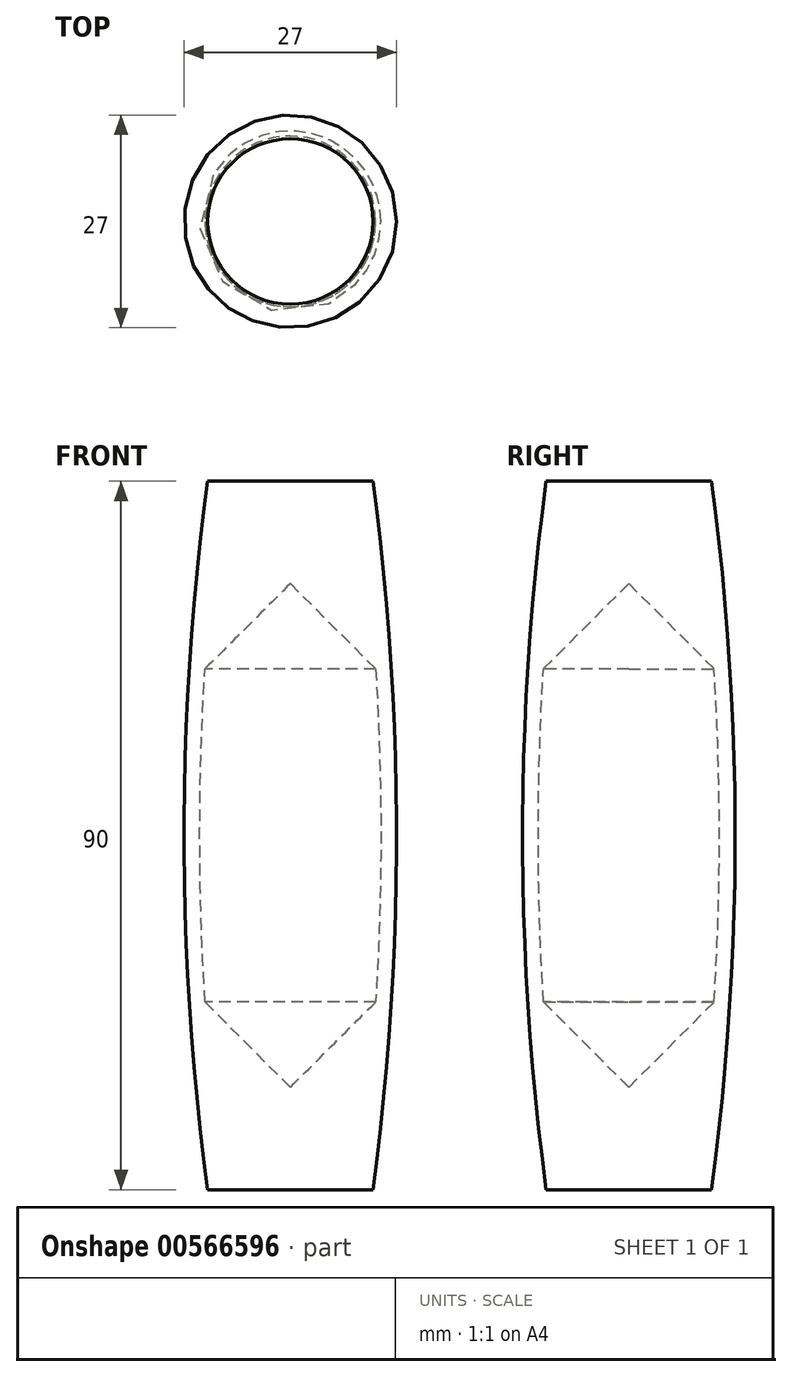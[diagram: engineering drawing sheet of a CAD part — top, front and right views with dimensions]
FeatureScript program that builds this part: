
annotation { "Feature Type Name" : "Feature", "Feature Type Description" : "" }
export const myFeature = defineFeature(function(context is Context, id is Id, definition is map)
    precondition{}
    {
        {
            var Q0;
            Q0=qCreatedBy(makeId("Front.planeOp"),FACE);
            var sketch = newSketch(context, id + "F0", { "sketchPlane" : qUnion([Q0])});
            skLineSegment(sketch, "E0", {"start": v(0, 45) * mm, "end": v(-10.5, 45) * mm});
            skLineSegment(sketch, "E1.MirrorCS", {"start": v(0, -45) * mm, "end": v(-10.5, -45) * mm});
            skArc(sketch, "E2", {"start": v(-10.5, 45) * mm, "mid": v(-13.5, 0) * mm, "end": v(-10.5, -45) * mm});
            skArc(sketch, "E3.0", {"start": v(-10.83, 21.17) * mm, "mid": v(-11.5, 0) * mm, "end": v(-10.83, -21.17) * mm});
            skLineSegment(sketch, "E4", {"start": v(0, 32) * mm, "end": v(-10.83, 21.17) * mm});
            skLineSegment(sketch, "E5.MirrorCS", {"start": v(0, -32) * mm, "end": v(-10.83, -21.17) * mm});
            skLineSegment(sketch, "E6", {"start": v(0, 45) * mm, "end": v(0, 32) * mm});
            skLineSegment(sketch, "E7.MirrorCS", {"start": v(0, -45) * mm, "end": v(0, -32) * mm});
            skSolve(sketch);
        }
        {
            var Q0;
            Q0 = qSketchRegion(id + "F0", true);
            var Q1;
            Q1=sQuery(id+"F0.wireOp",EDGE,"E6");
            revolve(context, id + "F1", {"entities" : qUnion([Q0]), "axis" : qUnion([Q1]), "revolveType" : RevolveType.FULL});
        }
    });
